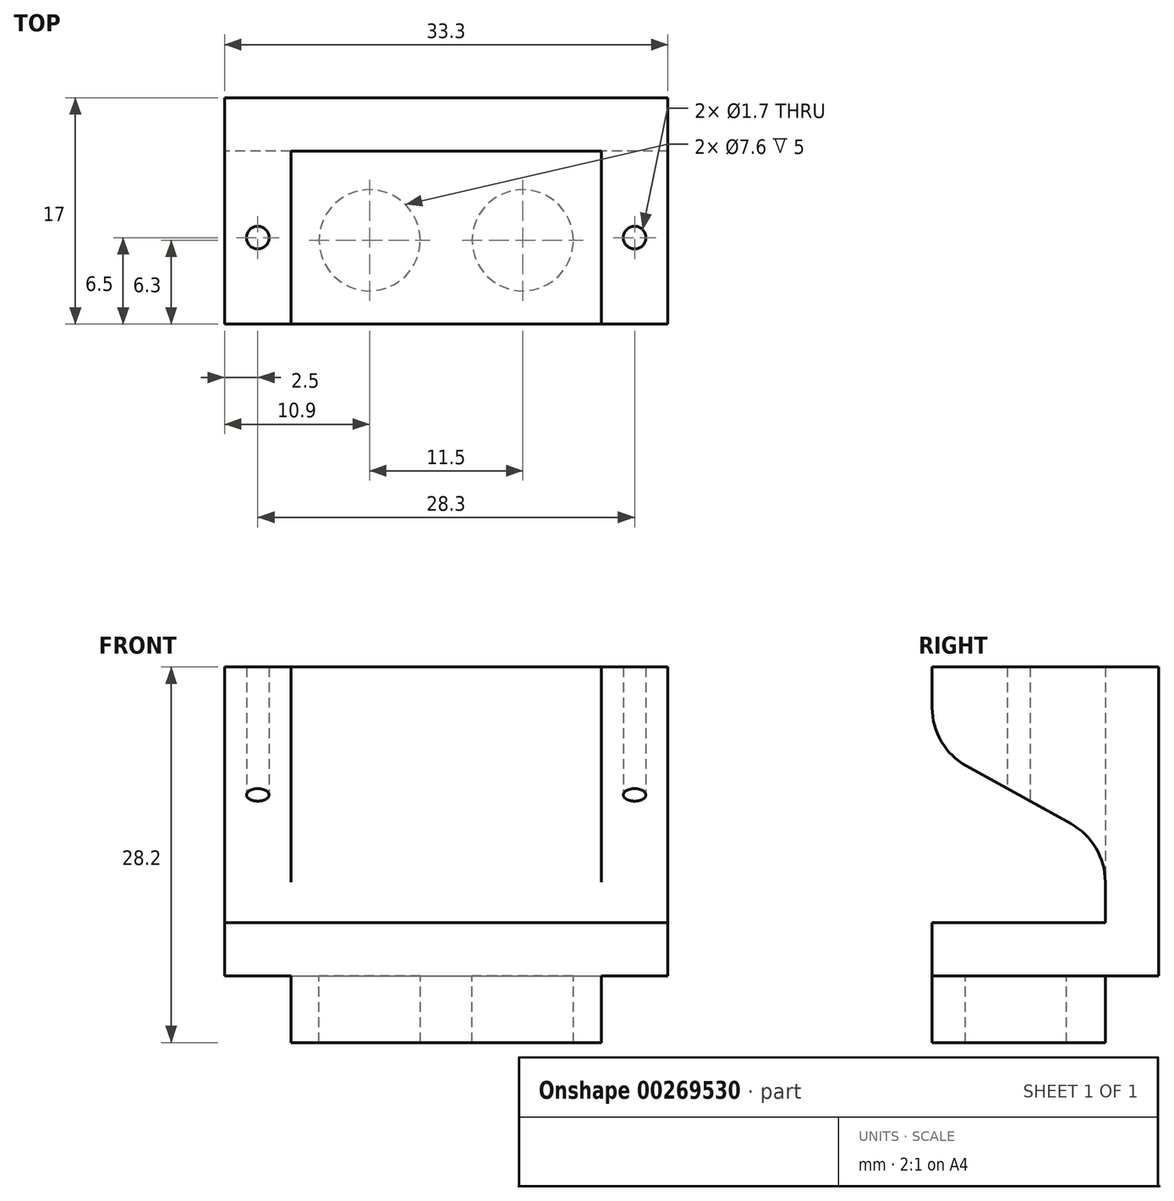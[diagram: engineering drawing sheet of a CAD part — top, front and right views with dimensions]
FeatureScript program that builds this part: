
annotation { "Feature Type Name" : "Feature", "Feature Type Description" : "" }
export const myFeature = defineFeature(function(context is Context, id is Id, definition is map)
    precondition{}
    {
        {
            var Q0;
            Q0=qCreatedBy(makeId("Top.planeOp"),FACE);
            var sketch = newSketch(context, id + "F0", { "sketchPlane" : qUnion([Q0])});
            skLineSegment(sketch, "E0.bottom", {"start": v(16.65, 8.5) * mm, "end": v(-16.65, 8.5) * mm});
            skLineSegment(sketch, "E0.top", {"start": v(16.65, -8.5) * mm, "end": v(-16.65, -8.5) * mm});
            skLineSegment(sketch, "E0.left", {"start": v(16.65, 8.5) * mm, "end": v(16.65, -8.5) * mm});
            skLineSegment(sketch, "E0.right", {"start": v(-16.65, 8.5) * mm, "end": v(-16.65, -8.5) * mm});
            skPoint(sketch, "E0.middle", {"position": v(0, 0) * mm});
            skLineSegment(sketch, "E1", {"start": v(11.65, -8.5) * mm, "end": v(11.65, 8.5) * mm});
            skLineSegment(sketch, "E2", {"start": v(-11.65, -8.5) * mm, "end": v(-11.65, 8.5) * mm});
            skLineSegment(sketch, "E3", {"start": v(-11.65, 4.5) * mm, "end": v(11.65, 4.5) * mm});
            skCircle(sketch, "E4", {"center": v(14.15, -2) * mm, "radius": 0.85 * mm});
            skCircle(sketch, "E5", {"center": v(-14.15, -2) * mm, "radius": 0.85 * mm});
            skCircle(sketch, "E6", {"center": v(-5.75, -2.2) * mm, "radius": 3.8 * mm});
            skCircle(sketch, "E7.MirrorC", {"center": v(5.75, -2.2) * mm, "radius": 3.8 * mm});
            skLineSegment(sketch, "E8.bottom", {"start": v(-16.65, 8.5) * mm, "end": v(-33.65, 8.5) * mm});
            skLineSegment(sketch, "E8.top", {"start": v(-16.65, -8.5) * mm, "end": v(-33.65, -8.5) * mm});
            skLineSegment(sketch, "E8.right", {"start": v(-33.65, 8.5) * mm, "end": v(-33.65, -8.5) * mm});
            skLineSegment(sketch, "E9.bottom", {"start": v(-16.65, 8.5) * mm, "end": v(16.65, 8.5) * mm});
            skLineSegment(sketch, "E9.top", {"start": v(-16.65, 25.5) * mm, "end": v(16.65, 25.5) * mm});
            skLineSegment(sketch, "E9.left", {"start": v(-16.65, 8.5) * mm, "end": v(-16.65, 25.5) * mm});
            skLineSegment(sketch, "E9.right", {"start": v(16.65, 8.5) * mm, "end": v(16.65, 25.5) * mm});
            skCircle(sketch, "E10", {"center": v(-25.15, 0) * mm, "radius": 3 * mm});
            skPoint(sketch, "E10.centerSnap0", {"position": v(-25.15, -8.5) * mm});
            skCircle(sketch, "E11", {"center": v(-8.33, 17) * mm, "radius": 3 * mm});
            skPoint(sketch, "E11.centerSnap0", {"position": v(-16.65, 17) * mm});
            skLineSegment(sketch, "E12", {"start": v(0, 25.5) * mm, "end": v(0, 8.5) * mm});
            skCircle(sketch, "E13.MirrorC", {"center": v(8.33, 17) * mm, "radius": 3 * mm});
            skSolve(sketch);
        }
        {
            var Q0;
            Q0=qCreatedBy(makeId("Front.planeOp"),FACE);
            var sketch = newSketch(context, id + "F1", { "sketchPlane" : qUnion([Q0])});
            skLineSegment(sketch, "E14.bottom", {"start": v(-16.65, 0) * mm, "end": v(16.65, 0) * mm});
            skLineSegment(sketch, "E14.top", {"start": v(-16.65, 23.2) * mm, "end": v(16.65, 23.2) * mm});
            skLineSegment(sketch, "E14.left", {"start": v(-16.65, 0) * mm, "end": v(-16.65, 23.2) * mm});
            skLineSegment(sketch, "E14.right", {"start": v(16.65, 0) * mm, "end": v(16.65, 23.2) * mm});
            skLineSegment(sketch, "E15", {"start": v(-16.65, 4) * mm, "end": v(16.65, 4) * mm});
            skLineSegment(sketch, "E16", {"start": v(11.65, 0) * mm, "end": v(11.65, 23.2) * mm});
            skLineSegment(sketch, "E17", {"start": v(-11.65, 0) * mm, "end": v(-11.65, 23.2) * mm});
            skLineSegment(sketch, "E18", {"start": v(16.65, 10) * mm, "end": v(11.65, 10) * mm});
            skLineSegment(sketch, "E19", {"start": v(-11.65, 10) * mm, "end": v(-16.65, 10) * mm});
            skLineSegment(sketch, "E20", {"start": v(11.65, 17.2) * mm, "end": v(16.65, 17.2) * mm});
            skLineSegment(sketch, "E21", {"start": v(-11.65, 17.2) * mm, "end": v(-16.65, 17.2) * mm});
            skSolve(sketch);
        }
        {
            var Q0;
            Q0=qCreatedBy(makeId("Right.planeOp"),FACE);
            var sketch = newSketch(context, id + "F2", { "sketchPlane" : qUnion([Q0])});
            skLineSegment(sketch, "E22.bottom", {"start": v(-8.5, 0) * mm, "end": v(8.5, 0) * mm});
            skLineSegment(sketch, "E22.top", {"start": v(-8.5, 23.2) * mm, "end": v(8.5, 23.2) * mm});
            skLineSegment(sketch, "E22.left", {"start": v(-8.5, 20.15) * mm, "end": v(-8.5, 23.2) * mm});
            skLineSegment(sketch, "E22.right", {"start": v(8.5, 0) * mm, "end": v(8.5, 23.2) * mm});
            skLineSegment(sketch, "E23", {"start": v(4.5, 7.05) * mm, "end": v(4.5, 0) * mm});
            skLineSegment(sketch, "E24", {"start": v(4.5, 17.2) * mm, "end": v(-8.5, 17.2) * mm});
            skLineSegment(sketch, "E25", {"start": v(4.5, 4) * mm, "end": v(-8.5, 4) * mm});
            skLineSegment(sketch, "E26", {"start": v(-8.5, 10) * mm, "end": v(4.5, 10) * mm});
            skLineSegment(sketch, "E27", {"start": v(-5.92, 15.77) * mm, "end": v(1.92, 11.43) * mm});
            skArc(sketch, "E28.filletArc", {"start": v(-8.5, 20.15) * mm, "mid": v(-7.8, 17.6) * mm, "end": v(-5.92, 15.77) * mm});
            skArc(sketch, "E29.filletArc", {"start": v(4.5, 7.05) * mm, "mid": v(3.8, 9.6) * mm, "end": v(1.92, 11.43) * mm});
            skLineSegment(sketch, "E30", {"start": v(-8.5, 20.15) * mm, "end": v(-8.5, 0) * mm});
            skSolve(sketch);
        }
        {
            var Q0;
            {var subQ0=sQuery(id+"F1.wireOp",EDGE,"E19");Q0=makeQuery(id+"F1.imprint","IMPRINT",FACE,{"disambiguationData":[TD([[makeQuery(id+"F1.imprint","IMPRINT",EDGE,{"derivedFrom":subQ0}),-1.0]])]});}
            var Q1;
            {var subQ5=sQuery(id+"F1.wireOp",EDGE,"E21");Q1=makeQuery(id+"F1.imprint","IMPRINT",FACE,{"disambiguationData":[TD([[makeQuery(id+"F1.imprint","IMPRINT",EDGE,{"derivedFrom":subQ5}),-1.0]])]});}
            var Q2;
            {var subQ3=sQuery(id+"F1.wireOp",EDGE,"E19");Q2=makeQuery(id+"F1.imprint","IMPRINT",FACE,{"disambiguationData":[TD([[makeQuery(id+"F1.imprint","IMPRINT",EDGE,{"derivedFrom":subQ3}),1.0]])]});}
            var Q3;
            {var subQ0=sQuery(id+"F1.wireOp",EDGE,"E14.left");var subQ1=sQuery(id+"F1.wireOp",EDGE,"E14.bottom");var subQ2=makeQuery(id+"F1.imprint","INTERSECT",VERTEX,{"derivedFrom":[subQ1,subQ0]});Q3=makeQuery(id+"F1.imprint","IMPRINT",FACE,{"disambiguationData":[TD([[makeQuery(id+"F1.imprint","IMPRINT",EDGE,{"disambiguationData":[TD([[subQ2,-1.0]])],"derivedFrom":subQ1}),1.0]])]});}
            var Q4;
            {var subQ0=sQuery(id+"F1.wireOp",EDGE,"E16");var subQ1=sQuery(id+"F1.wireOp",EDGE,"E14.bottom");var subQ2=makeQuery(id+"F1.imprint","INTERSECT",VERTEX,{"derivedFrom":[subQ1,subQ0]});Q4=makeQuery(id+"F1.imprint","IMPRINT",FACE,{"disambiguationData":[TD([[makeQuery(id+"F1.imprint","IMPRINT",EDGE,{"disambiguationData":[TD([[subQ2,1.0]])],"derivedFrom":subQ1}),1.0]])]});}
            var Q5;
            {var subQ0=sQuery(id+"F1.wireOp",EDGE,"E14.right");var subQ1=sQuery(id+"F1.wireOp",EDGE,"E14.bottom");var subQ2=makeQuery(id+"F1.imprint","INTERSECT",VERTEX,{"derivedFrom":[subQ1,subQ0]});Q5=makeQuery(id+"F1.imprint","IMPRINT",FACE,{"disambiguationData":[TD([[makeQuery(id+"F1.imprint","IMPRINT",EDGE,{"disambiguationData":[TD([[subQ2,1.0]])],"derivedFrom":subQ1}),1.0]])]});}
            var Q6;
            {var subQ3=sQuery(id+"F1.wireOp",EDGE,"E18");Q6=makeQuery(id+"F1.imprint","IMPRINT",FACE,{"disambiguationData":[TD([[makeQuery(id+"F1.imprint","IMPRINT",EDGE,{"derivedFrom":subQ3}),1.0]])]});}
            var Q7;
            {var subQ0=sQuery(id+"F1.wireOp",EDGE,"E18");Q7=makeQuery(id+"F1.imprint","IMPRINT",FACE,{"disambiguationData":[TD([[makeQuery(id+"F1.imprint","IMPRINT",EDGE,{"derivedFrom":subQ0}),-1.0]])]});}
            var Q8;
            {var subQ5=sQuery(id+"F1.wireOp",EDGE,"E20");Q8=makeQuery(id+"F1.imprint","IMPRINT",FACE,{"disambiguationData":[TD([[makeQuery(id+"F1.imprint","IMPRINT",EDGE,{"derivedFrom":subQ5}),1.0]])]});}
            extrude(context, id + "F3", {"entities" : qUnion([Q0, Q1, Q2, Q3, Q4, Q5, Q6, Q7, Q8]), "endBound" : BoundingType.SYMMETRIC, "depth" : 17 * mm});
        }
        {
            var Q0;
            {var subQ5=sQuery(id+"F0.wireOp",EDGE,"E3");Q0=makeQuery(id+"F0.imprint","IMPRINT",FACE,{"disambiguationData":[TD([[makeQuery(id+"F0.imprint","IMPRINT",EDGE,{"derivedFrom":subQ5}),1.0]])]});}
            extrude(context, id + "F4", {"entities" : qUnion([Q0]), "operationType" : NewBodyOperationType.ADD, "depth" : 23.2 * mm});
        }
        {
            var Q0;
            {var subQ0=sQuery(id+"F2.wireOp",EDGE,"E27");Q0=makeQuery(id+"F2.imprint","IMPRINT",FACE,{"disambiguationData":[TD([[makeQuery(id+"F2.imprint","IMPRINT",EDGE,{"derivedFrom":subQ0}),-1.0]])]});}
            var Q1;
            {var subQ0=sQuery(id+"F2.wireOp",EDGE,"E30");var subQ1=sQuery(id+"F2.wireOp",EDGE,"E24");var subQ2=makeQuery(id+"F2.imprint","INTERSECT",VERTEX,{"derivedFrom":[subQ1,subQ0]});Q1=makeQuery(id+"F2.imprint","IMPRINT",FACE,{"disambiguationData":[TD([[makeQuery(id+"F2.imprint","IMPRINT",EDGE,{"disambiguationData":[TD([[subQ2,1.0]])],"derivedFrom":subQ1}),-1.0]])]});}
            var Q2;
            {var subQ5=sQuery(id+"F2.wireOp",EDGE,"E25");Q2=makeQuery(id+"F2.imprint","IMPRINT",FACE,{"disambiguationData":[TD([[makeQuery(id+"F2.imprint","IMPRINT",EDGE,{"derivedFrom":subQ5}),-1.0]])]});}
            extrude(context, id + "F5", {"entities" : qUnion([Q0, Q1, Q2]), "operationType" : NewBodyOperationType.REMOVE, "endBound" : BoundingType.SYMMETRIC, "oppositeDirection" : true, "depth" : 36.2 * mm});
        }
        {
            var Q0;
            Q0=makeQuery(id+"F0.imprint","IMPRINT",FACE,{"disambiguationData":[TD([[makeQuery(id+"F0.imprint","IMPRINT",EDGE,{"derivedFrom":sQuery(id+"F0.wireOp",EDGE,"E4")}),1.0]])]});
            var Q1;
            Q1=makeQuery(id+"F0.imprint","IMPRINT",FACE,{"disambiguationData":[TD([[makeQuery(id+"F0.imprint","IMPRINT",EDGE,{"derivedFrom":sQuery(id+"F0.wireOp",EDGE,"E5")}),1.0]])]});
            extrude(context, id + "F6", {"entities" : qUnion([Q0, Q1]), "operationType" : NewBodyOperationType.REMOVE, "depth" : 25 * mm, "hasSecondDirection" : true, "secondDirectionOppositeDirection" : false, "secondDirectionDepth" : 4.3 * mm});
        }
        {
            var Q0;
            Q0=makeQuery(id+"F0.imprint","IMPRINT",FACE,{"disambiguationData":[TD([[makeQuery(id+"F0.imprint","IMPRINT",EDGE,{"derivedFrom":sQuery(id+"F0.wireOp",EDGE,"E7.MirrorC")}),-1.0]])]});
            extrude(context, id + "F7", {"entities" : qUnion([Q0]), "operationType" : NewBodyOperationType.ADD, "oppositeDirection" : true, "depth" : 5 * mm});
        }
    });
